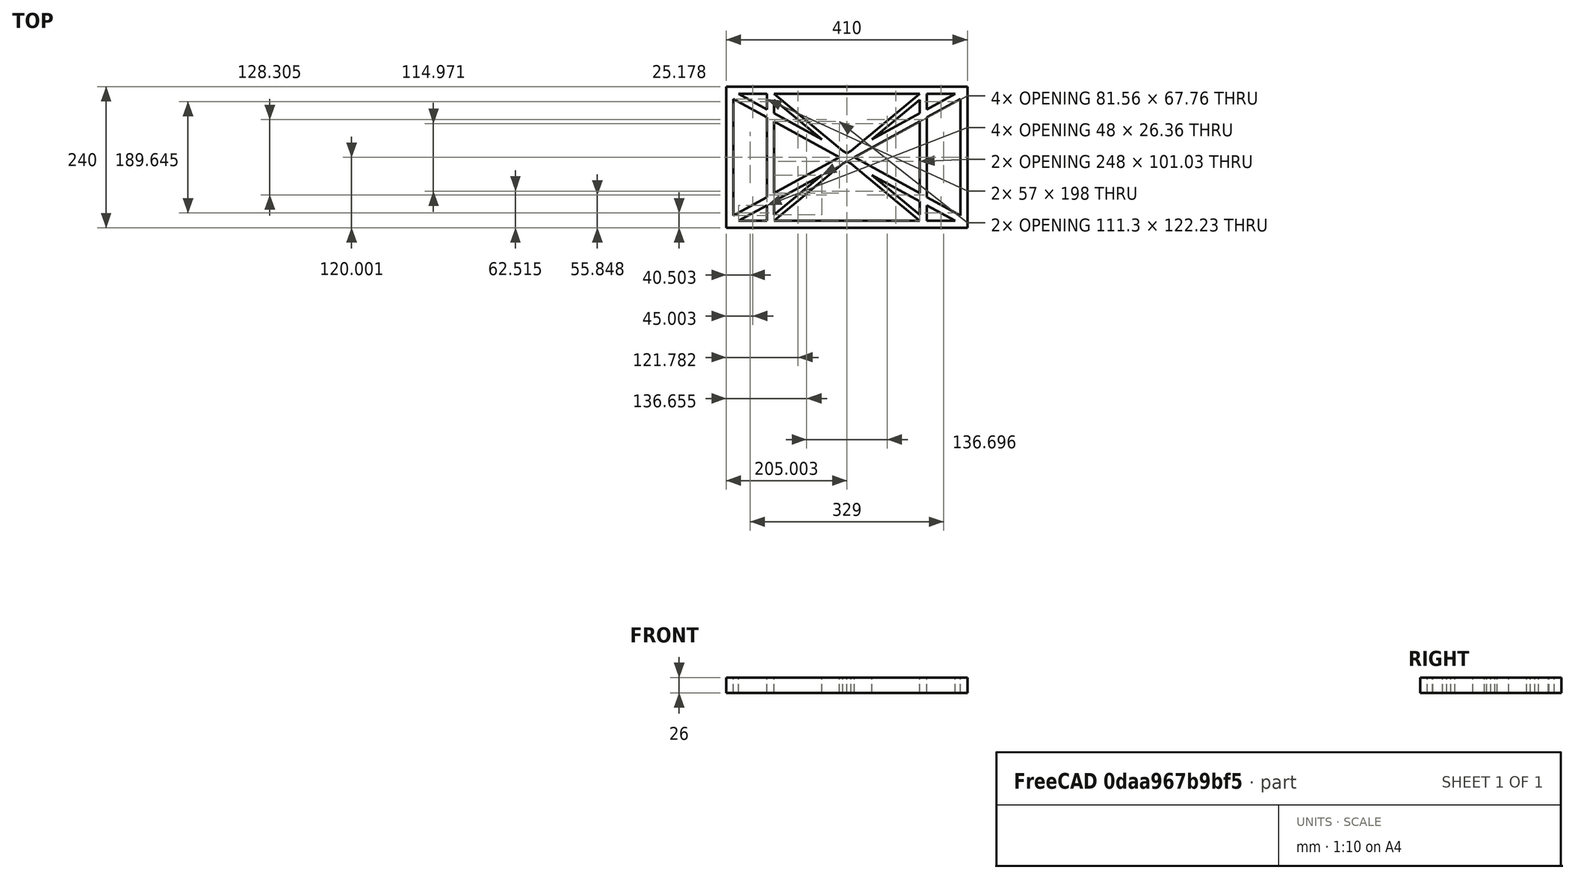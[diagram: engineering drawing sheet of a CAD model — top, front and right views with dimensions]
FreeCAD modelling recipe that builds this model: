
FCSTD DOCUMENT  (FreeCAD 0.19R0.19.2)
Label: laptopStand021
License: All rights reserved
LicenseURL: http://en.wikipedia.org/wiki/All_rights_reserved
objects: Sketcher::SketchObject×3, Part::Extrusion×1
note: 4 computed .brp shape members not serialized (recipe doc carries the construction recipe); baked Part::Feature solids carry a one-line shape summary decoded from their .brp

FEATURE [Sketcher::SketchObject] Sketch
  FullyConstrained = true
  sketch-geometry (52):
    g0: LineSegment StartX=-22.9272 StartY=136.221 StartZ=0 EndX=-22.9272 EndY=-103.779 EndZ=0
    g1: LineSegment StartX=-22.9272 StartY=136.221 StartZ=0 EndX=387.073 EndY=136.221 EndZ=0
    g2: LineSegment StartX=-22.9272 StartY=-103.779 StartZ=0 EndX=387.073 EndY=-103.779 EndZ=0
    g3: LineSegment StartX=387.073 StartY=136.221 StartZ=0 EndX=387.073 EndY=-103.779 EndZ=0
    g4: LineSegment StartX=375.073 StartY=115.221 StartZ=0 EndX=318.073 EndY=83.9235 EndZ=0
    g5: LineSegment StartX=-10.9272 StartY=-82.7794 StartZ=0 EndX=46.0728 EndY=-51.4823 EndZ=0
    g6: LineSegment StartX=-1.92719 StartY=124.221 StartZ=0 EndX=46.0728 EndY=97.8651 EndZ=0
    g7: LineSegment StartX=366.073 StartY=-91.7794 StartZ=0 EndX=318.073 EndY=-65.424 EndZ=0
    g8: LineSegment StartX=-10.9272 StartY=115.221 StartZ=0 EndX=-10.9272 EndY=-82.7794 EndZ=0
    g9: LineSegment StartX=375.073 StartY=-82.7794 StartZ=0 EndX=375.073 EndY=115.221 EndZ=0
    g10: LineSegment StartX=-1.92719 StartY=-91.7794 StartZ=0 EndX=46.0728 EndY=-91.7794 EndZ=0
    g11: LineSegment StartX=318.073 StartY=124.221 StartZ=0 EndX=366.073 EndY=124.221 EndZ=0
    g12: LineSegment StartX=306.073 StartY=-81.8102 StartZ=0 EndX=224.513 EndY=-14.0532 EndZ=0
    g13: LineSegment StartX=58.0728 StartY=114.251 StartZ=0 EndX=139.632 EndY=46.4944 EndZ=0
    g14: LineSegment StartX=306.073 StartY=124.221 StartZ=0 EndX=189.124 EndY=27.0628 EndZ=0
    g15: LineSegment StartX=58.0728 StartY=-91.7794 StartZ=0 EndX=175.022 EndY=5.37834 EndZ=0
    g16: LineSegment StartX=46.0728 StartY=124.221 StartZ=0 EndX=46.0728 EndY=97.8651 EndZ=0
    g17: LineSegment StartX=58.0728 StartY=-81.8102 StartZ=0 EndX=58.0728 EndY=-58.8351 EndZ=0
    g18: LineSegment StartX=318.073 StartY=124.221 StartZ=0 EndX=318.073 EndY=97.8651 EndZ=0
    g19: LineSegment StartX=306.073 StartY=114.251 StartZ=0 EndX=306.073 EndY=91.2763 EndZ=0
    g20: LineSegment StartX=182.073 StartY=23.1914 StartZ=0 EndX=189.124 EndY=27.0628 EndZ=0
    g21: LineSegment StartX=182.073 StartY=9.24976 StartZ=0 EndX=175.022 EndY=5.37834 EndZ=0
    g22: LineSegment StartX=224.513 StartY=46.4944 StartZ=0 EndX=306.073 EndY=114.251 EndZ=0
    g23: LineSegment StartX=175.022 StartY=27.0628 StartZ=0 EndX=58.0728 EndY=124.221 EndZ=0
    g24: LineSegment StartX=169.377 StartY=16.2206 StartZ=0 EndX=58.0728 EndY=77.3346 EndZ=0
    g25: LineSegment StartX=139.632 StartY=-14.0532 StartZ=0 EndX=58.0728 EndY=-81.8102 EndZ=0
    g26: LineSegment StartX=194.768 StartY=16.2206 StartZ=0 EndX=306.073 EndY=-44.8935 EndZ=0
    g27: LineSegment StartX=224.513 StartY=46.4944 StartZ=0 EndX=306.073 EndY=91.2763 EndZ=0
    g28: LineSegment StartX=175.022 StartY=27.0628 StartZ=0 EndX=182.073 EndY=23.1914 EndZ=0
    g29: LineSegment StartX=139.632 StartY=-14.0532 StartZ=0 EndX=58.0728 EndY=-58.8351 EndZ=0
    g30: LineSegment StartX=189.124 StartY=5.37834 StartZ=0 EndX=182.073 EndY=9.24976 EndZ=0
    g31: LineSegment StartX=189.124 StartY=5.37834 StartZ=0 EndX=306.073 EndY=-91.7794 EndZ=0
    g32: LineSegment StartX=306.073 StartY=77.3346 StartZ=0 EndX=306.073 EndY=-44.8935 EndZ=0
    g33: LineSegment StartX=318.073 StartY=83.9235 StartZ=0 EndX=318.073 EndY=-51.4823 EndZ=0
    g34: LineSegment StartX=318.073 StartY=97.8651 StartZ=0 EndX=366.073 EndY=124.221 EndZ=0
    g35: LineSegment StartX=306.073 StartY=77.3346 StartZ=0 EndX=194.768 EndY=16.2206 EndZ=0
    g36: LineSegment StartX=306.073 StartY=-58.8351 StartZ=0 EndX=224.513 EndY=-14.0532 EndZ=0
    g37: LineSegment StartX=306.073 StartY=-58.8351 StartZ=0 EndX=306.073 EndY=-81.8102 EndZ=0
    g38: LineSegment StartX=318.073 StartY=-51.4823 StartZ=0 EndX=375.073 EndY=-82.7794 EndZ=0
    g39: LineSegment StartX=318.073 StartY=-65.424 StartZ=0 EndX=318.073 EndY=-91.7794 EndZ=0
    g40: LineSegment StartX=306.073 StartY=124.221 StartZ=0 EndX=58.0728 EndY=124.221 EndZ=0
    g41: LineSegment StartX=318.073 StartY=-91.7794 StartZ=0 EndX=366.073 EndY=-91.7794 EndZ=0
    g42: LineSegment StartX=58.0728 StartY=-91.7794 StartZ=0 EndX=306.073 EndY=-91.7794 EndZ=0
    g43: LineSegment StartX=58.0728 StartY=-44.8935 StartZ=0 EndX=58.0728 EndY=77.3346 EndZ=0
    g44: LineSegment StartX=46.0728 StartY=-65.424 StartZ=0 EndX=-1.92719 EndY=-91.7794 EndZ=0
    g45: LineSegment StartX=46.0728 StartY=-65.424 StartZ=0 EndX=46.0728 EndY=-91.7794 EndZ=0
    g46: LineSegment StartX=58.0728 StartY=-44.8935 StartZ=0 EndX=169.377 EndY=16.2206 EndZ=0
    g47: LineSegment StartX=58.0728 StartY=91.2763 StartZ=0 EndX=58.0728 EndY=114.251 EndZ=0
    g48: LineSegment StartX=46.0728 StartY=83.9235 StartZ=0 EndX=46.0728 EndY=-51.4823 EndZ=0
    g49: LineSegment StartX=46.0728 StartY=124.221 StartZ=0 EndX=-1.92719 EndY=124.221 EndZ=0
    g50: LineSegment StartX=58.0728 StartY=91.2763 StartZ=0 EndX=139.632 EndY=46.4944 EndZ=0
    g51: LineSegment StartX=46.0728 StartY=83.9235 StartZ=0 EndX=-10.9272 EndY=115.221 EndZ=0
  constraints (102):
    c: Vertical(g0)
    c: Distance(g0) = 240
    c: Horizontal(g1)
    c: Distance(g1) = 410
    c: Coincident(g1,g0)
    c: Coincident(g2,g0)
    c: Horizontal(g2)
    c: Coincident(g3,g1)
    c: Vertical(g3)
    c: Coincident(g2,g3)
    c: Block(g1)
    c: Horizontal(g10)
    c: Horizontal(g11)
    c: PointOnObject(g35,g6)
    c: Coincident(g28,g20)
    c: Coincident(g30,g21)
    c: Tangent(g7,g24)
    c: PointOnObject(g24,g5)
    c: PointOnObject(g26,g4)
    c: Coincident(g20,g14)
    c: Tangent(g20,g27)
    c: Coincident(g50,g13)
    c: Coincident(g28,g23)
    c: Coincident(g22,g27)
    c: Coincident(g21,g15)
    c: Coincident(g29,g25)
    c: Tangent(g21,g29)
    c: Coincident(g36,g12)
    c: Coincident(g31,g30)
    c: Coincident(g22,g19)
    c: Tangent(g19,g32)
    c: Tangent(g18,g33)
    c: Coincident(g27,g19)
    c: Tangent(g27,g34)
    c: Coincident(g4,g33)
    c: Coincident(g35,g32)
    c: Tangent(g4,g35)
    c: Coincident(g37,g12)
    c: Tangent(g7,g36)
    c: Tangent(g32,g37)
    c: Coincident(g26,g32)
    c: Tangent(g26,g38)
    c: Coincident(g33,g38)
    c: Coincident(g39,g7)
    c: Tangent(g33,g39)
    c: Coincident(g25,g17)
    c: Tangent(g17,g43)
    c: Coincident(g29,g17)
    c: Tangent(g29,g44)
    c: Coincident(g45,g44)
    c: Tangent(g16,g45)
    c: Coincident(g5,g48)
    c: Coincident(g46,g43)
    c: Tangent(g5,g46)
    c: Tangent(g43,g47)
    c: Tangent(g16,g48)
    c: Coincident(g13,g47)
    c: PointOnObject(g40,g23)
    c: Tangent(g40,g49)
    c: Coincident(g6,g16)
    c: Coincident(g50,g47)
    c: Tangent(g6,g50)
    c: Coincident(g24,g43)
    c: Coincident(g51,g48)
    c: Tangent(g24,g51)
    c: Block(g23)
    c: Block(g14)
    c: Block(g20)
    c: Block(g40)
    c: Block(g18)
    c: Block(g34)
    c: Block(g4)
    c: Block(g38)
    c: Block(g9)
    c: Block(g36)
    c: Block(g37)
    c: Block(g7)
    c: Block(g39)
    c: Block(g22)
    c: Block(g31)
    c: Block(g42)
    c: Block(g21)
    c: Block(g15)
    c: Block(g29)
    c: Block(g25)
    c: Block(g45)
    c: Block(g44)
    c: Block(g5)
    c: Block(g8)
    c: Block(g51)
    c: Block(g6)
    c: Block(g16)
    c: Block(g13)
    c: Block(g47)
    c: Block(g35)
    c: Block(g32)
    c: Block(g24)
    c: Block(g46)
    c: Block(g49)
    c: Block(g11)
    c: Block(g41)
    c: Block(g10)
FEATURE [Part::Extrusion] Extrude
  Base = -> Sketch
  Dir = (0,0,1)
  DirMode = 2
  FaceMakerClass = Part::FaceMakerBullseye
  LengthFwd = 26
  LengthRev = 0
  Solid = true
  Symmetric = false
FEATURE [Sketcher::SketchObject] Sketch001
  FullyConstrained = false
  MapMode = 4
  Placement = pos=(0,0,0) rot=(0.57735,0.57735,0.57735;2.0944rad)
  Support = -> [Sketch]
  sketch-geometry (15):
    g0: LineSegment StartX=17.2228 StartY=-16.0875 StartZ=0 EndX=117.223 EndY=-16.0875 EndZ=0
    g1: LineSegment StartX=17.2228 StartY=-16.0875 StartZ=0 EndX=17.2228 EndY=-19.0875 EndZ=0
    g2: LineSegment StartX=117.223 StartY=-16.0875 StartZ=0 EndX=117.223 EndY=-19.0875 EndZ=0
    g3: BSplineCurve PolesCount=3 KnotsCount=2 Degree=2 IsPeriodic=0
    g4: LineSegment StartX=94.6577 StartY=-26.1351 StartZ=0 EndX=24.2583 EndY=-213.335 EndZ=0
    g5: LineSegment StartX=-9.4377 StartY=-200.664 StartZ=0 EndX=24.2583 EndY=-213.335 EndZ=0
    g6: LineSegment StartX=-9.4377 StartY=-200.664 StartZ=0 EndX=56.1962 EndY=-26.1351 EndZ=0
    g7: LineSegment StartX=17.2228 StartY=-19.0875 StartZ=0 EndX=38.8094 EndY=-19.0875 EndZ=0
    g8: BSplineCurve PolesCount=4 KnotsCount=2 Degree=3 IsPeriodic=0
    g9: LineSegment StartX=56.1962 StartY=-26.1351 StartZ=0 EndX=58.7648 EndY=-19.3049 EndZ=0
    g10: LineSegment StartX=94.6577 StartY=-26.1351 StartZ=0 EndX=97.3081 EndY=-19.0875 EndZ=0
    g11: LineSegment StartX=58.7648 StartY=-19.3049 StartZ=0 EndX=78.0148 EndY=-19.3049 EndZ=0
    g12: LineSegment StartX=78.0148 StartY=-19.3049 StartZ=0 EndX=65.3429 EndY=-53.001 EndZ=0
    g13: LineSegment StartX=65.3429 StartY=-53.001 StartZ=0 EndX=53.1749 EndY=-48.425 EndZ=0
    g14: LineSegment StartX=65.3429 StartY=-53.001 StartZ=0 EndX=77.5109 EndY=-57.5769 EndZ=0
  constraints (39):
    c: Horizontal(g0)
    c: Distance(g0) = 100
    c: Block(g0)
    c: Coincident(g1,g0)
    c: Vertical(g1)
    c: Distance(g1) = 3
    c: Coincident(g2,g0)
    c: Vertical(g2)
    c: Distance(g2) = 3
    c: Block(g3)
    c: Coincident(g3,g2)
    c: Coincident(g4,g3)
    c: Block(g4)
    c: Coincident(g5,g4)
    c: Parallel(g4,g6)
    c: Coincident(g6,g5)
    c: Coincident(g7,g1)
    c: Horizontal(g7)
    c: Block(g8)
    c: Coincident(g8,g7)
    c: Coincident(g8,g6)
    c: Block(g6)
    c: Coincident(g9,g6)
    c: Parallel(g9,g6)
    c: Coincident(g10,g3)
    c: Parallel(g10,g4)
    c: Coincident(g11,g9)
    c: Horizontal(g11)
    c: Distance(g11) = 19.25
    c: Coincident(g12,g11)
    c: Distance(g12) = 36
    c: Block(g9)
    c: Parallel(g4,g12)
    c: Coincident(g13,g12)
    c: Distance(g13) = 13
    c: Coincident(g14,g12)
    c: Distance(g14) = 13
    c: Perpendicular(g14,g12)
    c: Perpendicular(g12,g13)
FEATURE [Sketcher::SketchObject] Sketch002
  FullyConstrained = true
  Placement = pos=(0,0,0) rot=(-1,0,0;4.71239rad)
